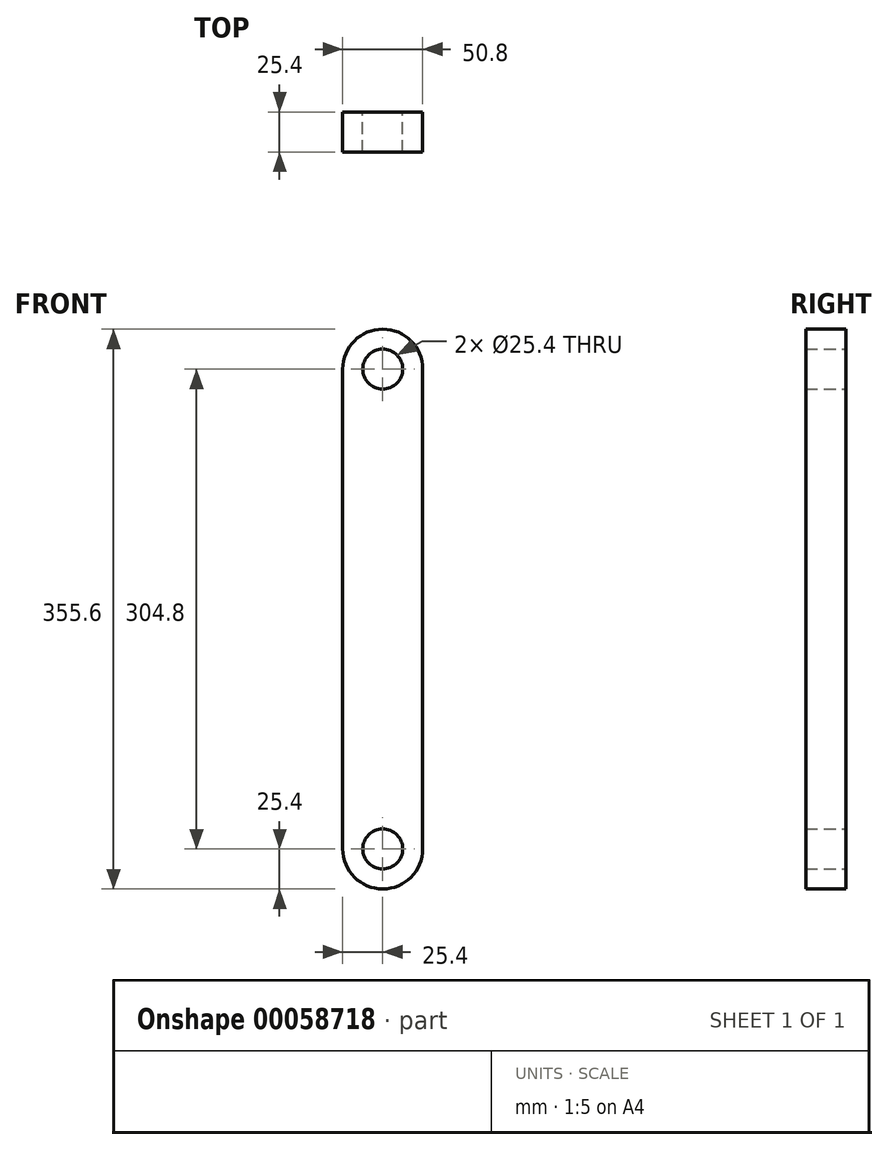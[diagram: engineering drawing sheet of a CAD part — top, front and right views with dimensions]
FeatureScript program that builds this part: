
annotation { "Feature Type Name" : "Feature", "Feature Type Description" : "" }
export const myFeature = defineFeature(function(context is Context, id is Id, definition is map)
    precondition{}
    {
        {
            var Q0;
            Q0=qCreatedBy(makeId("Front.planeOp"),FACE);
            var sketch = newSketch(context, id + "F0", { "sketchPlane" : qUnion([Q0])});
            skCircle(sketch, "E0", {"center": v(0, 0) * mm, "radius": 12.7 * mm});
            skArc(sketch, "E1", {"start": v(25.4, 0) * mm, "mid": v(0, 25.4) * mm, "end": v(-25.4, 0) * mm});
            skCircle(sketch, "E2", {"center": v(0, -304.8) * mm, "radius": 12.7 * mm});
            skArc(sketch, "E3", {"start": v(-25.4, -304.8) * mm, "mid": v(0, -330.2) * mm, "end": v(25.4, -304.8) * mm});
            skLineSegment(sketch, "E4", {"start": v(-25.4, 0) * mm, "end": v(-25.4, -304.8) * mm});
            skLineSegment(sketch, "E5", {"start": v(25.4, 0) * mm, "end": v(25.4, -304.8) * mm});
            skSolve(sketch);
        }
        {
            var Q0;
            Q0=makeQuery(id+"F0.imprint","IMPRINT",FACE,{"disambiguationData":[TD([[makeQuery(id+"F0.imprint","IMPRINT",EDGE,{"derivedFrom":sQuery(id+"F0.wireOp",EDGE,"E0")}),-1.0]])]});
            extrude(context, id + "F1", {"entities" : qUnion([Q0]), "depth" : 25.4 * mm});
        }
    });
